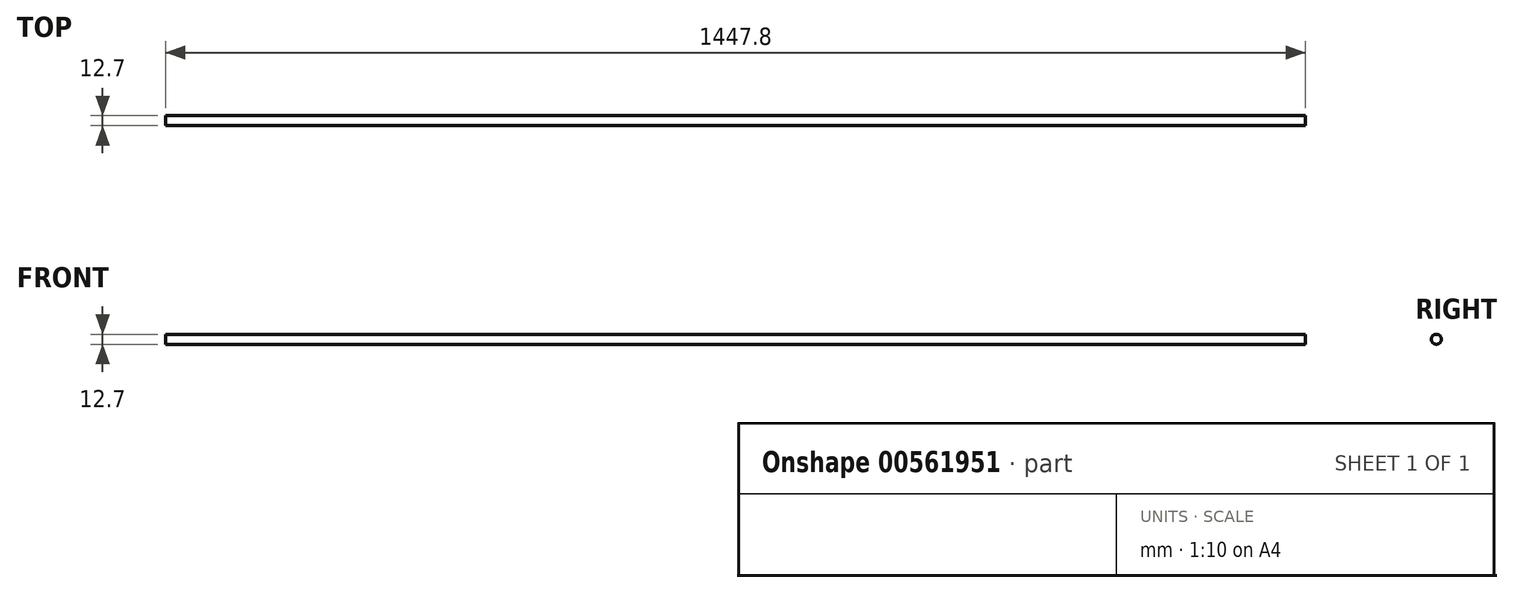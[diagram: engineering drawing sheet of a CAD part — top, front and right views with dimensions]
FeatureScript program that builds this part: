
annotation { "Feature Type Name" : "Feature", "Feature Type Description" : "" }
export const myFeature = defineFeature(function(context is Context, id is Id, definition is map)
    precondition{}
    {
        {
            var Q0;
            Q0=qCreatedBy(makeId("Right.planeOp"),FACE);
            var sketch = newSketch(context, id + "F0", { "sketchPlane" : qUnion([Q0])});
            skCircle(sketch, "E0", {"center": v(0, 0) * mm, "radius": 6.35 * mm});
            skSolve(sketch);
        }
        {
            var Q0;
            Q0 = qSketchRegion(id + "F0", true);
            extrude(context, id + "F1", {"entities" : qUnion([Q0]), "depth" : 1447.8 * mm, "offsetDistance" : 25.4 * mm, "symmetric" : true});
        }
    });
